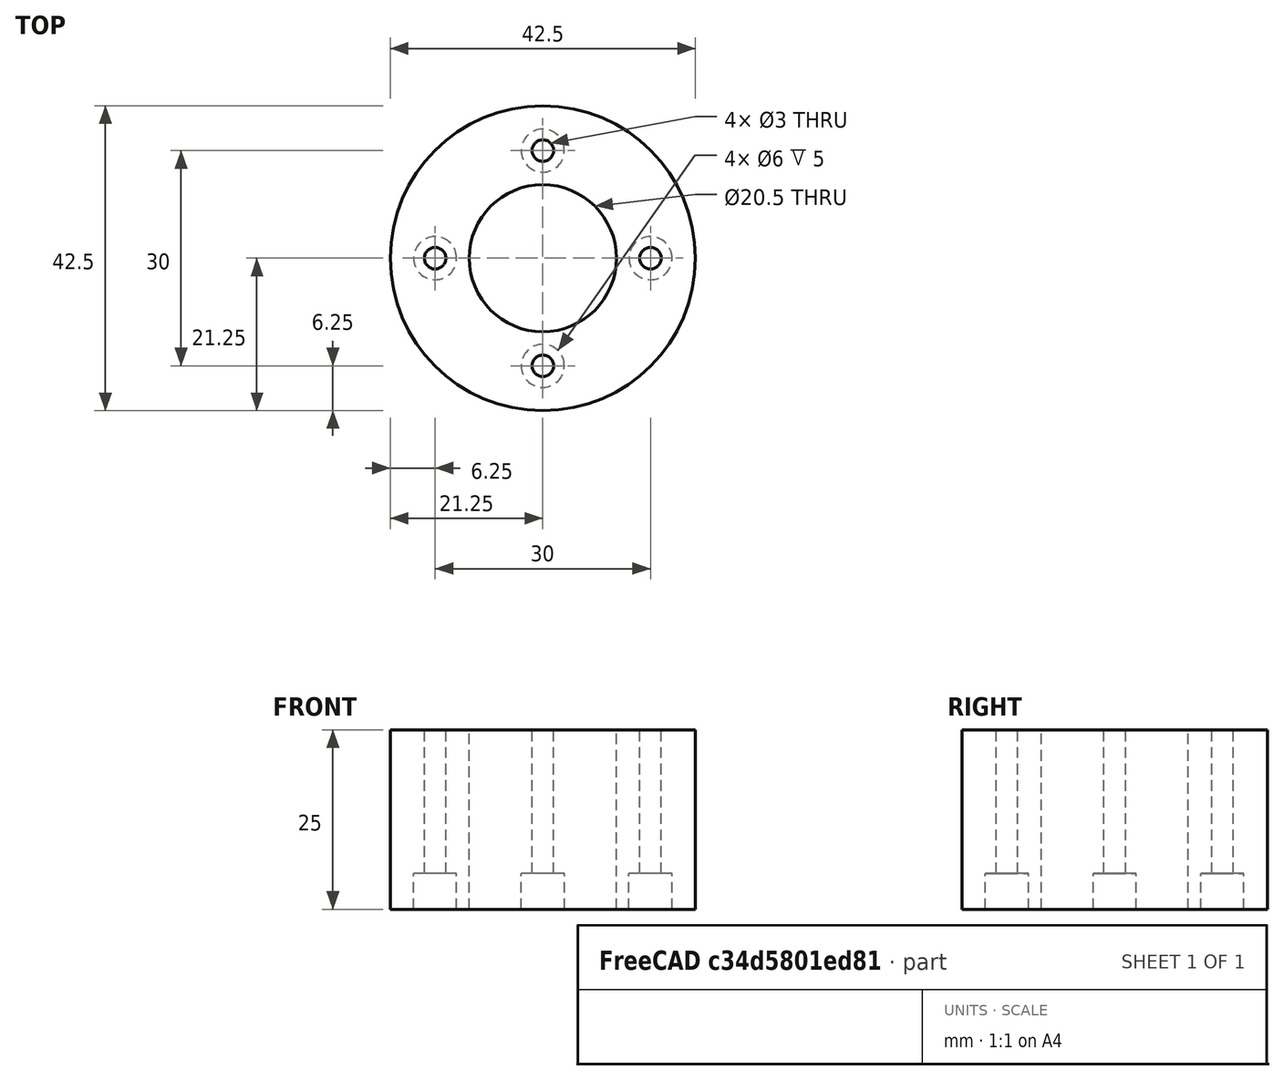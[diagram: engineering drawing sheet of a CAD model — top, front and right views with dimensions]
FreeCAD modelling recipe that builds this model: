
FCSTD DOCUMENT  (FreeCAD 0.17RUnknown)
Label: bohrklemm
License: All rights reserved
LicenseURL: http://en.wikipedia.org/wiki/All_rights_reserved
objects: Part::Cylinder×10, Part::Cut×9
note: 19 computed .brp shape members not serialized (recipe doc carries the construction recipe); baked Part::Feature solids carry a one-line shape summary decoded from their .brp

FEATURE [Part::Cylinder] Cylinder  label="Zylinder"
  Angle = 360
  AttacherType = Attacher::AttachEngine3D
  Height = 25
  Radius = 21.25
FEATURE [Part::Cylinder] Cylinder001  label="Zylinder001"
  Angle = 360
  AttacherType = Attacher::AttachEngine3D
  Height = 25
  Radius = 10.25
FEATURE [Part::Cylinder] Cylinder002  label="Zylinder002"
  Angle = 360
  AttacherType = Attacher::AttachEngine3D
  Height = 25
  Placement = pos=(15,0,0) rot=(0,0,1;0rad)
  Radius = 1.5
FEATURE [Part::Cylinder] Cylinder003  label="Zylinder003"
  Angle = 360
  AttacherType = Attacher::AttachEngine3D
  Height = 25
  Placement = pos=(0,15,0) rot=(0,0,1;0rad)
  Radius = 1.5
FEATURE [Part::Cylinder] Cylinder004  label="Zylinder004"
  Angle = 360
  AttacherType = Attacher::AttachEngine3D
  Height = 25
  Placement = pos=(-15,0,0) rot=(0,0,1;0rad)
  Radius = 1.5
FEATURE [Part::Cylinder] Cylinder005  label="Zylinder005"
  Angle = 360
  AttacherType = Attacher::AttachEngine3D
  Height = 25
  Placement = pos=(0,-15,0) rot=(0,0,1;0rad)
  Radius = 1.5
FEATURE [Part::Cut] Cut
  Base = -> Cylinder
  Tool = -> Cylinder001
FEATURE [Part::Cut] Cut001
  Base = -> Cut
  Tool = -> Cylinder002
FEATURE [Part::Cut] Cut002
  Base = -> Cut001
  Tool = -> Cylinder003
FEATURE [Part::Cut] Cut003
  Base = -> Cut002
  Tool = -> Cylinder004
FEATURE [Part::Cut] Cut004
  Base = -> Cut003
  Tool = -> Cylinder005
FEATURE [Part::Cylinder] Cylinder006  label="Zylinder006"
  Angle = 360
  AttacherType = Attacher::AttachEngine3D
  Height = 5
  Placement = pos=(15,0,0) rot=(0,0,1;0rad)
  Radius = 3
FEATURE [Part::Cylinder] Cylinder007  label="Zylinder007"
  Angle = 360
  AttacherType = Attacher::AttachEngine3D
  Height = 5
  Placement = pos=(0,15,0) rot=(0,0,1;0rad)
  Radius = 3
FEATURE [Part::Cylinder] Cylinder008  label="Zylinder008"
  Angle = 360
  AttacherType = Attacher::AttachEngine3D
  Height = 5
  Placement = pos=(-15,0,0) rot=(0,0,1;0rad)
  Radius = 3
FEATURE [Part::Cylinder] Cylinder009  label="Zylinder009"
  Angle = 360
  AttacherType = Attacher::AttachEngine3D
  Height = 5
  Placement = pos=(0,-15,0) rot=(0,0,1;0rad)
  Radius = 3
FEATURE [Part::Cut] Cut005
  Base = -> Cut004
  Tool = -> Cylinder006
FEATURE [Part::Cut] Cut006
  Base = -> Cut005
  Tool = -> Cylinder009
FEATURE [Part::Cut] Cut007
  Base = -> Cut006
  Tool = -> Cylinder008
FEATURE [Part::Cut] Cut008
  Base = -> Cut007
  Tool = -> Cylinder007
